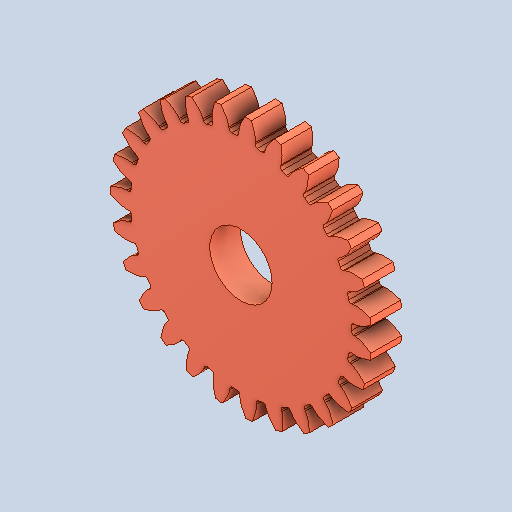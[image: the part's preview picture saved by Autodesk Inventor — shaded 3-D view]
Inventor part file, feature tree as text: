
AUTODESK INVENTOR PART (.ipt)
format: ipt  version: 2022 (Build 260153000, 153)  size: 462,336 bytes
history: imported  units: in
note: dims shown in document units (in); Inventor stores cm internally (conversion verified against a paired STEP export)
features: imported_body x1
ambient origin geometry x8: Origin, YZ Plane, XZ Plane, XY Plane, X Axis, Y Axis, Z Axis, Center Point
bodies: Solid1 (imported_parasolid), Body1 (imported_parasolid)
feature tree (1):
  imported_body  NMx_Import_Brep_tag  [imported B-rep: ~17 faces, bbox_mm=[14.641861, 8.264478, 3.1242]]
